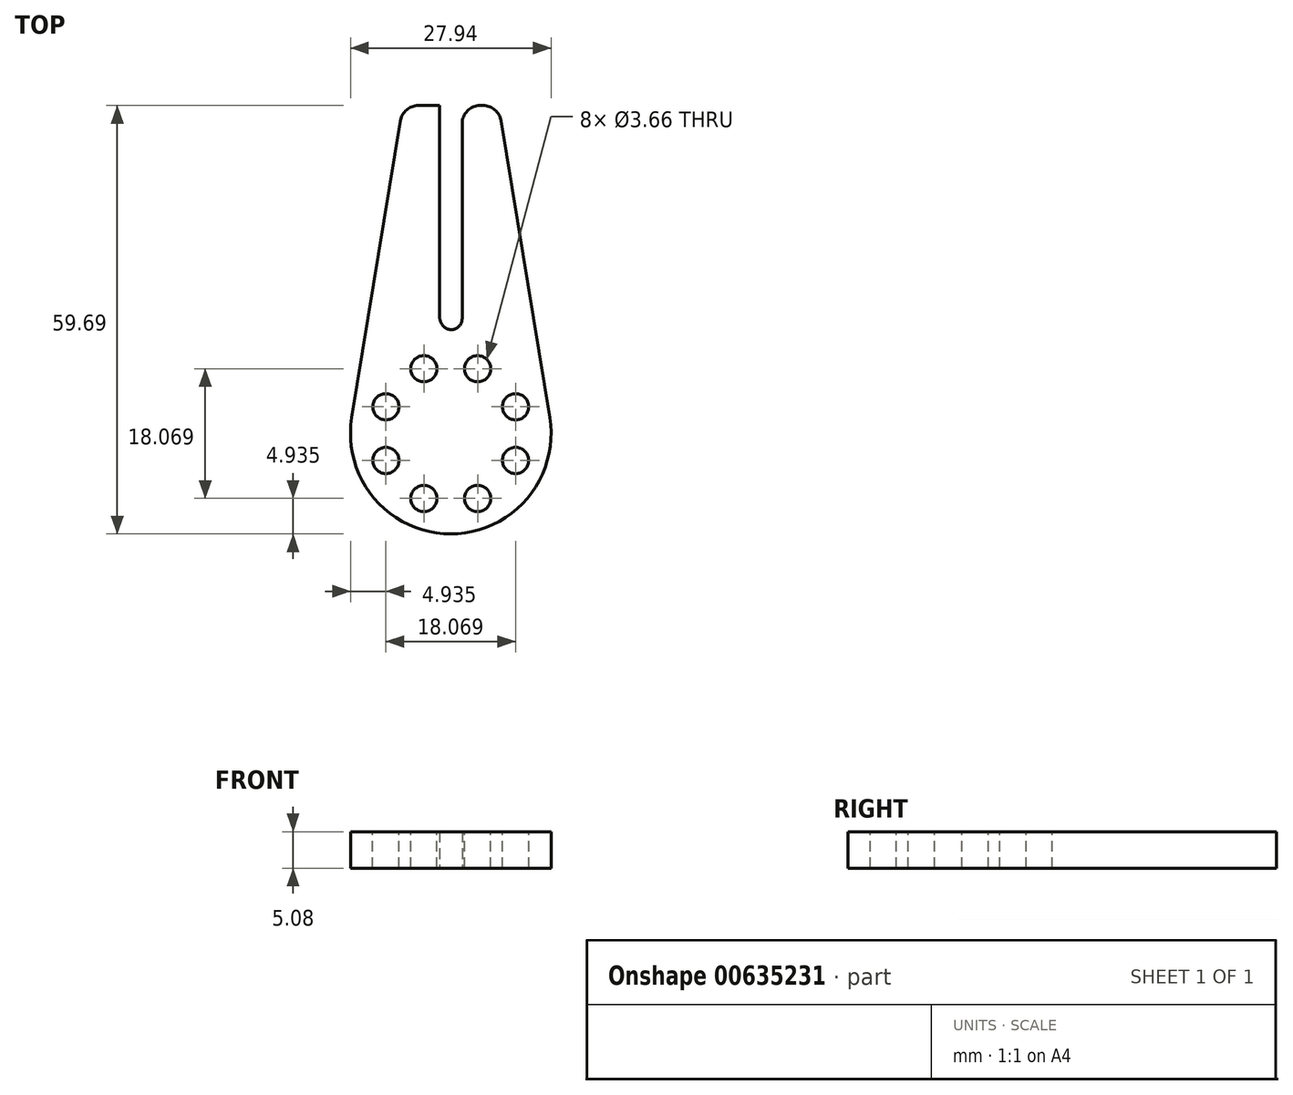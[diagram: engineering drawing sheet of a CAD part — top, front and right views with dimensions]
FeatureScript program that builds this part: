
annotation { "Feature Type Name" : "Feature", "Feature Type Description" : "" }
export const myFeature = defineFeature(function(context is Context, id is Id, definition is map)
    precondition{}
    {
        {
            var Q0;
            Q0=qCreatedBy(makeId("Top.planeOp"),FACE);
            var sketch = newSketch(context, id + "F0", { "sketchPlane" : qUnion([Q0])});
            skCircle(sketch, "E0", {"center": v(0, 0) * mm, "radius": 13.97 * mm});
            skLineSegment(sketch, "E1.bottom", {"start": v(-1.59, 45.72) * mm, "end": v(1.59, 45.72) * mm});
            skLineSegment(sketch, "E1.top", {"start": v(-1.59, 13.97) * mm, "end": v(1.59, 13.97) * mm});
            skLineSegment(sketch, "E1.left", {"start": v(-1.59, 45.72) * mm, "end": v(-1.59, 13.97) * mm});
            skLineSegment(sketch, "E1.right", {"start": v(1.59, 45.72) * mm, "end": v(1.59, 13.97) * mm});
            skPoint(sketch, "E2", {"position": v(0, 45.72) * mm});
            skPoint(sketch, "E3", {"position": v(0, 13.97) * mm});
            skLineSegment(sketch, "E4", {"start": v(-13.79, 2.26) * mm, "end": v(13.79, 2.26) * mm, "construction": true});
            skLineSegment(sketch, "E5", {"start": v(-1.59, 45.72) * mm, "end": v(-6.67, 45.72) * mm});
            skLineSegment(sketch, "E6", {"start": v(-6.67, 45.72) * mm, "end": v(1.59, 45.72) * mm});
            skLineSegment(sketch, "E7", {"start": v(1.59, 45.72) * mm, "end": v(6.67, 45.72) * mm});
            skLineSegment(sketch, "E8", {"start": v(-6.67, 45.72) * mm, "end": v(-13.79, 2.26) * mm});
            skLineSegment(sketch, "E9", {"start": v(13.97, 0) * mm, "end": v(-13.97, 0) * mm, "construction": true});
            skLineSegment(sketch, "E10", {"start": v(6.67, 45.72) * mm, "end": v(13.79, 2.26) * mm});
            skSolve(sketch);
        }
        {
            var Q0;
            Q0=makeQuery(id+"F0.imprint","IMPRINT",FACE,{"disambiguationData":[TD([[makeQuery(id+"F0.imprint","IMPRINT",EDGE,{"derivedFrom":sQuery(id+"F0.wireOp",EDGE,"E0")}),1.0]])]});
            var Q1;
            {var subQ4=sQuery(id+"F0.wireOp",EDGE,"E1.left");Q1=makeQuery(id+"F0.imprint","IMPRINT",FACE,{"disambiguationData":[TD([[makeQuery(id+"F0.imprint","IMPRINT",EDGE,{"derivedFrom":subQ4}),-1.0]])]});}
            var Q2;
            {var subQ4=sQuery(id+"F0.wireOp",EDGE,"E1.right");Q2=makeQuery(id+"F0.imprint","IMPRINT",FACE,{"disambiguationData":[TD([[makeQuery(id+"F0.imprint","IMPRINT",EDGE,{"derivedFrom":subQ4}),1.0]])]});}
            extrude(context, id + "F1", {"entities" : qUnion([Q0, Q1, Q2]), "depth" : 5.08 * mm, "offsetDistance" : 25.4 * mm});
        }
        {
            var Q0;
            Q0=makeQuery(id+"F1.opExtrude","CAP_FACE",FACE,{"disambiguationData":[OSD([sQuery(id+"F0.wireOp",EDGE,"E0"),sQuery(id+"F0.wireOp",EDGE,"E1.top"),sQuery(id+"F0.wireOp",EDGE,"E1.left"),sQuery(id+"F0.wireOp",EDGE,"E1.right"),sQuery(id+"F0.wireOp",EDGE,"dqpQMvVN-wCbQ-fHpb-S8bv-lJLQ9SVM9UzP"),sQuery(id+"F0.wireOp",EDGE,"L23oQJ8n-NyzH-ZTGg-QMos-f0L9qtsCzSFl")])],"isStart":false});
            var sketch = newSketch(context, id + "F2", { "sketchPlane" : qUnion([Q0])});
            skCircle(sketch, "E11.cCircle", {"center": v(0, 0) * mm, "radius": 9.03 * mm, "construction": true});
            skLineSegment(sketch, "E11.0", {"start": v(9.03, 3.74) * mm, "end": v(9.03, -3.74) * mm});
            skLineSegment(sketch, "E11.1", {"start": v(9.03, -3.74) * mm, "end": v(3.74, -9.03) * mm});
            skLineSegment(sketch, "E11.2", {"start": v(3.74, -9.03) * mm, "end": v(-3.74, -9.03) * mm});
            skLineSegment(sketch, "E11.3", {"start": v(-3.74, -9.03) * mm, "end": v(-9.03, -3.74) * mm});
            skLineSegment(sketch, "E11.4", {"start": v(-9.03, -3.74) * mm, "end": v(-9.03, 3.74) * mm});
            skLineSegment(sketch, "E11.5", {"start": v(-9.03, 3.74) * mm, "end": v(-3.74, 9.03) * mm});
            skLineSegment(sketch, "E11.6", {"start": v(-3.74, 9.03) * mm, "end": v(3.74, 9.03) * mm});
            skLineSegment(sketch, "E11.7", {"start": v(3.74, 9.03) * mm, "end": v(9.03, 3.74) * mm});
            skPoint(sketch, "E11.0.midPoint", {"position": v(9.03, 0) * mm});
            skCircle(sketch, "E12", {"center": v(-3.74, 9.03) * mm, "radius": 1.83 * mm});
            skCircle(sketch, "E13", {"center": v(3.74, 9.03) * mm, "radius": 1.83 * mm});
            skCircle(sketch, "E14", {"center": v(9.03, 3.74) * mm, "radius": 1.83 * mm});
            skCircle(sketch, "E15", {"center": v(9.03, -3.74) * mm, "radius": 1.83 * mm});
            skCircle(sketch, "E16", {"center": v(3.74, -9.03) * mm, "radius": 1.83 * mm});
            skCircle(sketch, "E17", {"center": v(-3.74, -9.03) * mm, "radius": 1.83 * mm});
            skCircle(sketch, "E18", {"center": v(-9.03, -3.74) * mm, "radius": 1.83 * mm});
            skCircle(sketch, "E19", {"center": v(-9.03, 3.74) * mm, "radius": 1.83 * mm});
            skSolve(sketch);
        }
        {
            var Q0;
            {var subQ0=sQuery(id+"F2.wireOp",EDGE,"E11.6");var subQ1=sQuery(id+"F2.wireOp",EDGE,"E11.5");var subQ2=makeQuery(id+"F2.imprint","INTERSECT",VERTEX,{"derivedFrom":[subQ1,subQ0]});Q0=makeQuery(id+"F2.imprint","IMPRINT",FACE,{"disambiguationData":[TD([[makeQuery(id+"F2.imprint","IMPRINT",EDGE,{"disambiguationData":[TD([[subQ2,1.0]])],"derivedFrom":subQ1}),1.0]])]});}
            var Q1;
            {var subQ0=sQuery(id+"F2.wireOp",EDGE,"E11.6");var subQ1=sQuery(id+"F2.wireOp",EDGE,"E11.5");var subQ2=makeQuery(id+"F2.imprint","INTERSECT",VERTEX,{"derivedFrom":[subQ1,subQ0]});Q1=makeQuery(id+"F2.imprint","IMPRINT",FACE,{"disambiguationData":[TD([[makeQuery(id+"F2.imprint","IMPRINT",EDGE,{"disambiguationData":[TD([[subQ2,1.0]])],"derivedFrom":subQ1}),-1.0]])]});}
            var Q2;
            {var subQ0=sQuery(id+"F2.wireOp",EDGE,"E11.7");var subQ1=sQuery(id+"F2.wireOp",EDGE,"E11.6");var subQ2=makeQuery(id+"F2.imprint","INTERSECT",VERTEX,{"derivedFrom":[subQ1,subQ0]});Q2=makeQuery(id+"F2.imprint","IMPRINT",FACE,{"disambiguationData":[TD([[makeQuery(id+"F2.imprint","IMPRINT",EDGE,{"disambiguationData":[TD([[subQ2,1.0]])],"derivedFrom":subQ1}),1.0]])]});}
            var Q3;
            {var subQ0=sQuery(id+"F2.wireOp",EDGE,"E11.7");var subQ1=sQuery(id+"F2.wireOp",EDGE,"E11.6");var subQ2=makeQuery(id+"F2.imprint","INTERSECT",VERTEX,{"derivedFrom":[subQ1,subQ0]});Q3=makeQuery(id+"F2.imprint","IMPRINT",FACE,{"disambiguationData":[TD([[makeQuery(id+"F2.imprint","IMPRINT",EDGE,{"disambiguationData":[TD([[subQ2,1.0]])],"derivedFrom":subQ1}),-1.0]])]});}
            var Q4;
            {var subQ0=sQuery(id+"F2.wireOp",EDGE,"E11.7");var subQ1=sQuery(id+"F2.wireOp",EDGE,"E11.0");var subQ2=makeQuery(id+"F2.imprint","INTERSECT",VERTEX,{"derivedFrom":[subQ1,subQ0]});Q4=makeQuery(id+"F2.imprint","IMPRINT",FACE,{"disambiguationData":[TD([[makeQuery(id+"F2.imprint","IMPRINT",EDGE,{"disambiguationData":[TD([[subQ2,-1.0]])],"derivedFrom":subQ1}),1.0]])]});}
            var Q5;
            {var subQ0=sQuery(id+"F2.wireOp",EDGE,"E11.7");var subQ1=sQuery(id+"F2.wireOp",EDGE,"E11.0");var subQ2=makeQuery(id+"F2.imprint","INTERSECT",VERTEX,{"derivedFrom":[subQ1,subQ0]});Q5=makeQuery(id+"F2.imprint","IMPRINT",FACE,{"disambiguationData":[TD([[makeQuery(id+"F2.imprint","IMPRINT",EDGE,{"disambiguationData":[TD([[subQ2,-1.0]])],"derivedFrom":subQ1}),-1.0]])]});}
            var Q6;
            {var subQ0=sQuery(id+"F2.wireOp",EDGE,"E11.1");var subQ1=sQuery(id+"F2.wireOp",EDGE,"E11.0");var subQ2=makeQuery(id+"F2.imprint","INTERSECT",VERTEX,{"derivedFrom":[subQ1,subQ0]});Q6=makeQuery(id+"F2.imprint","IMPRINT",FACE,{"disambiguationData":[TD([[makeQuery(id+"F2.imprint","IMPRINT",EDGE,{"disambiguationData":[TD([[subQ2,1.0]])],"derivedFrom":subQ1}),1.0]])]});}
            var Q7;
            {var subQ0=sQuery(id+"F2.wireOp",EDGE,"E11.1");var subQ1=sQuery(id+"F2.wireOp",EDGE,"E11.0");var subQ2=makeQuery(id+"F2.imprint","INTERSECT",VERTEX,{"derivedFrom":[subQ1,subQ0]});Q7=makeQuery(id+"F2.imprint","IMPRINT",FACE,{"disambiguationData":[TD([[makeQuery(id+"F2.imprint","IMPRINT",EDGE,{"disambiguationData":[TD([[subQ2,1.0]])],"derivedFrom":subQ1}),-1.0]])]});}
            var Q8;
            {var subQ0=sQuery(id+"F2.wireOp",EDGE,"E11.2");var subQ1=sQuery(id+"F2.wireOp",EDGE,"E11.1");var subQ2=makeQuery(id+"F2.imprint","INTERSECT",VERTEX,{"derivedFrom":[subQ1,subQ0]});Q8=makeQuery(id+"F2.imprint","IMPRINT",FACE,{"disambiguationData":[TD([[makeQuery(id+"F2.imprint","IMPRINT",EDGE,{"disambiguationData":[TD([[subQ2,1.0]])],"derivedFrom":subQ1}),1.0]])]});}
            var Q9;
            {var subQ0=sQuery(id+"F2.wireOp",EDGE,"E11.2");var subQ1=sQuery(id+"F2.wireOp",EDGE,"E11.1");var subQ2=makeQuery(id+"F2.imprint","INTERSECT",VERTEX,{"derivedFrom":[subQ1,subQ0]});Q9=makeQuery(id+"F2.imprint","IMPRINT",FACE,{"disambiguationData":[TD([[makeQuery(id+"F2.imprint","IMPRINT",EDGE,{"disambiguationData":[TD([[subQ2,1.0]])],"derivedFrom":subQ1}),-1.0]])]});}
            var Q10;
            {var subQ0=sQuery(id+"F2.wireOp",EDGE,"E11.3");var subQ1=sQuery(id+"F2.wireOp",EDGE,"E11.2");var subQ2=makeQuery(id+"F2.imprint","INTERSECT",VERTEX,{"derivedFrom":[subQ1,subQ0]});Q10=makeQuery(id+"F2.imprint","IMPRINT",FACE,{"disambiguationData":[TD([[makeQuery(id+"F2.imprint","IMPRINT",EDGE,{"disambiguationData":[TD([[subQ2,1.0]])],"derivedFrom":subQ1}),1.0]])]});}
            var Q11;
            {var subQ0=sQuery(id+"F2.wireOp",EDGE,"E11.3");var subQ1=sQuery(id+"F2.wireOp",EDGE,"E11.2");var subQ2=makeQuery(id+"F2.imprint","INTERSECT",VERTEX,{"derivedFrom":[subQ1,subQ0]});Q11=makeQuery(id+"F2.imprint","IMPRINT",FACE,{"disambiguationData":[TD([[makeQuery(id+"F2.imprint","IMPRINT",EDGE,{"disambiguationData":[TD([[subQ2,1.0]])],"derivedFrom":subQ1}),-1.0]])]});}
            var Q12;
            {var subQ0=sQuery(id+"F2.wireOp",EDGE,"E11.4");var subQ1=sQuery(id+"F2.wireOp",EDGE,"E11.3");var subQ2=makeQuery(id+"F2.imprint","INTERSECT",VERTEX,{"derivedFrom":[subQ1,subQ0]});Q12=makeQuery(id+"F2.imprint","IMPRINT",FACE,{"disambiguationData":[TD([[makeQuery(id+"F2.imprint","IMPRINT",EDGE,{"disambiguationData":[TD([[subQ2,1.0]])],"derivedFrom":subQ1}),-1.0]])]});}
            var Q13;
            {var subQ0=sQuery(id+"F2.wireOp",EDGE,"E11.4");var subQ1=sQuery(id+"F2.wireOp",EDGE,"E11.3");var subQ2=makeQuery(id+"F2.imprint","INTERSECT",VERTEX,{"derivedFrom":[subQ1,subQ0]});Q13=makeQuery(id+"F2.imprint","IMPRINT",FACE,{"disambiguationData":[TD([[makeQuery(id+"F2.imprint","IMPRINT",EDGE,{"disambiguationData":[TD([[subQ2,1.0]])],"derivedFrom":subQ1}),1.0]])]});}
            var Q14;
            {var subQ0=sQuery(id+"F2.wireOp",EDGE,"E11.5");var subQ1=sQuery(id+"F2.wireOp",EDGE,"E11.4");var subQ2=makeQuery(id+"F2.imprint","INTERSECT",VERTEX,{"derivedFrom":[subQ1,subQ0]});Q14=makeQuery(id+"F2.imprint","IMPRINT",FACE,{"disambiguationData":[TD([[makeQuery(id+"F2.imprint","IMPRINT",EDGE,{"disambiguationData":[TD([[subQ2,1.0]])],"derivedFrom":subQ1}),1.0]])]});}
            var Q15;
            {var subQ0=sQuery(id+"F2.wireOp",EDGE,"E11.5");var subQ1=sQuery(id+"F2.wireOp",EDGE,"E11.4");var subQ2=makeQuery(id+"F2.imprint","INTERSECT",VERTEX,{"derivedFrom":[subQ1,subQ0]});Q15=makeQuery(id+"F2.imprint","IMPRINT",FACE,{"disambiguationData":[TD([[makeQuery(id+"F2.imprint","IMPRINT",EDGE,{"disambiguationData":[TD([[subQ2,1.0]])],"derivedFrom":subQ1}),-1.0]])]});}
            extrude(context, id + "F3", {"entities" : qUnion([Q0, Q1, Q2, Q3, Q4, Q5, Q6, Q7, Q8, Q9, Q10, Q11, Q12, Q13, Q14, Q15]), "operationType" : NewBodyOperationType.REMOVE, "oppositeDirection" : true, "depth" : 25.4 * mm, "offsetDistance" : 25.4 * mm});
        }
        {
            var Q0;
            Q0=makeQuery(id+"F1.opExtrude","SWEPT_EDGE",EDGE,{"disambiguationData":[OSD([sQuery(id+"F0.wireOp",EDGE,"E7"),sQuery(id+"F0.wireOp",EDGE,"Hb75mWoy-3Bym-SXzH-b3La-NYSZENcDcdJU")])]});
            var Q1;
            Q1=makeQuery(id+"F1.opExtrude","SWEPT_EDGE",EDGE,{"disambiguationData":[OSD([sQuery(id+"F0.wireOp",EDGE,"E1.right"),sQuery(id+"F0.wireOp",EDGE,"E6"),sQuery(id+"F0.wireOp",EDGE,"E7")])]});
            var Q2;
            Q2=makeQuery(id+"F1.opExtrude","SWEPT_EDGE",EDGE,{"disambiguationData":[OSD([sQuery(id+"F0.wireOp",EDGE,"E1.left"),sQuery(id+"F0.wireOp",EDGE,"E6")])]});
            var Q3;
            Q3=makeQuery(id+"F1.opExtrude","SWEPT_EDGE",EDGE,{"disambiguationData":[OSD([sQuery(id+"F0.wireOp",EDGE,"E6"),sQuery(id+"F0.wireOp",EDGE,"E8")])]});
            fillet(context, id + "F4", {"entities" : qUnion([Q0, Q1, Q2, Q3]), "radius" : 2.54 * mm, "tangentPropagation" : true, "allowEdgeOverflow" : false});
        }
        {
            var Q0;
            Q0=makeQuery(id+"F1.opExtrude","SWEPT_EDGE",EDGE,{"disambiguationData":[OSD([sQuery(id+"F0.wireOp",EDGE,"E1.top"),sQuery(id+"F0.wireOp",EDGE,"E1.left")])]});
            var Q1;
            Q1=makeQuery(id+"F1.opExtrude","SWEPT_EDGE",EDGE,{"disambiguationData":[OSD([sQuery(id+"F0.wireOp",EDGE,"E1.top"),sQuery(id+"F0.wireOp",EDGE,"E1.right")])]});
            fillet(context, id + "F5", {"entities" : qUnion([Q0, Q1]), "radius" : 1.52 * mm, "tangentPropagation" : true, "allowEdgeOverflow" : false});
        }
    });
